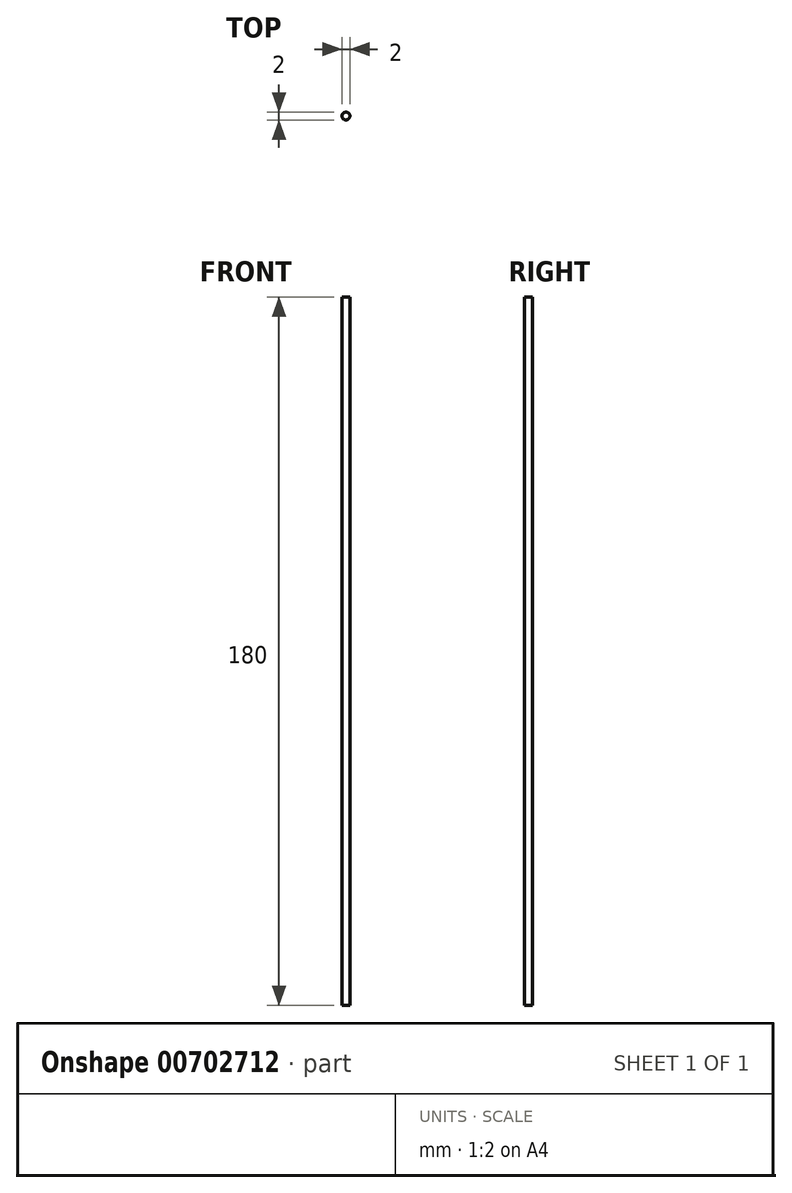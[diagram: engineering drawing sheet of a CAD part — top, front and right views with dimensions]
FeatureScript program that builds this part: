
annotation { "Feature Type Name" : "Feature", "Feature Type Description" : "" }
export const myFeature = defineFeature(function(context is Context, id is Id, definition is map)
    precondition{}
    {
        {
            var Q0;
            Q0=qCreatedBy(makeId("Top.planeOp"),FACE);
            var sketch = newSketch(context, id + "F0", { "sketchPlane" : qUnion([Q0])});
            skCircle(sketch, "E0", {"center": v(0, 0) * mm, "radius": 1 * mm});
            skSolve(sketch);
        }
        {
            var Q0;
            Q0=makeQuery(id+"F0.imprint","IMPRINT",FACE,{"disambiguationData":[TD([[makeQuery(id+"F0.imprint","IMPRINT",EDGE,{"derivedFrom":sQuery(id+"F0.wireOp",EDGE,"E0")}),1.0]])]});
            extrude(context, id + "F1", {"entities" : qUnion([Q0]), "depth" : 180 * mm, "offsetDistance" : 25.4 * mm});
        }
    });
